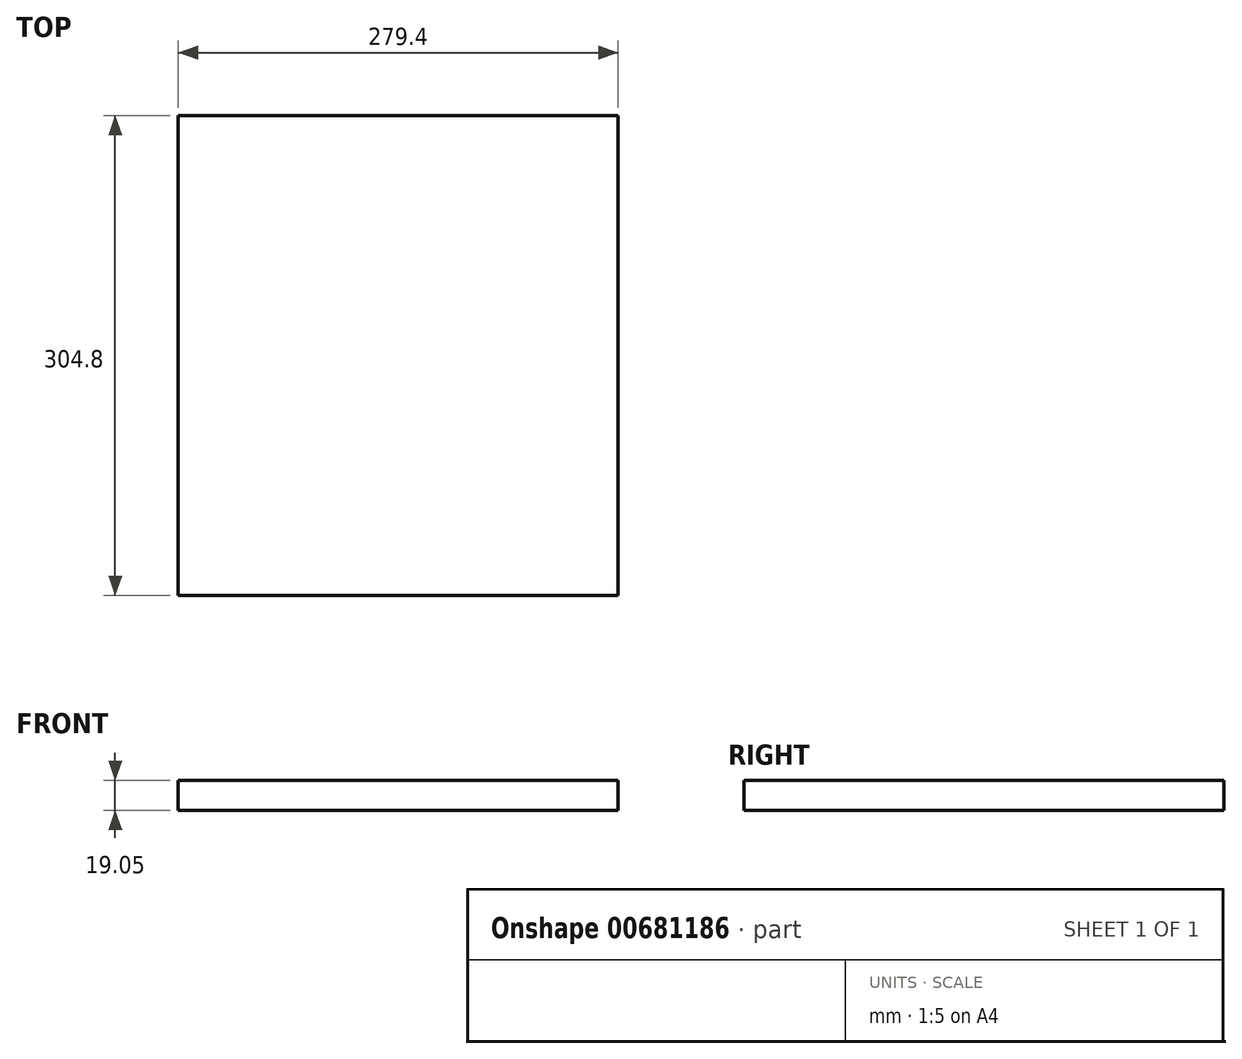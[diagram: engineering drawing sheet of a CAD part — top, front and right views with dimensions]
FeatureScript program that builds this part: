
annotation { "Feature Type Name" : "Feature", "Feature Type Description" : "" }
export const myFeature = defineFeature(function(context is Context, id is Id, definition is map)
    precondition{}
    {
        {
            var Q0;
            Q0=qCreatedBy(makeId("Top.planeOp"),FACE);
            var sketch = newSketch(context, id + "F0", { "sketchPlane" : qUnion([Q0])});
            skLineSegment(sketch, "E0.bottom", {"start": v(-139.7, 152.4) * mm, "end": v(139.7, 152.4) * mm});
            skLineSegment(sketch, "E0.top", {"start": v(-139.7, -152.4) * mm, "end": v(139.7, -152.4) * mm});
            skLineSegment(sketch, "E0.left", {"start": v(-139.7, 152.4) * mm, "end": v(-139.7, -152.4) * mm});
            skLineSegment(sketch, "E0.right", {"start": v(139.7, 152.4) * mm, "end": v(139.7, -152.4) * mm});
            skPoint(sketch, "E0.middle", {"position": v(0, 0) * mm});
            skSolve(sketch);
        }
        {
            var Q0;
            Q0=makeQuery(id+"F0.imprint","IMPRINT",FACE,{"disambiguationData":[TD([[makeQuery(id+"F0.imprint","IMPRINT",EDGE,{"derivedFrom":sQuery(id+"F0.wireOp",EDGE,"E0.bottom")}),-1.0]])]});
            extrude(context, id + "F1", {"entities" : qUnion([Q0]), "depth" : 19.05 * mm, "offsetDistance" : 25.4 * mm});
        }
    });
